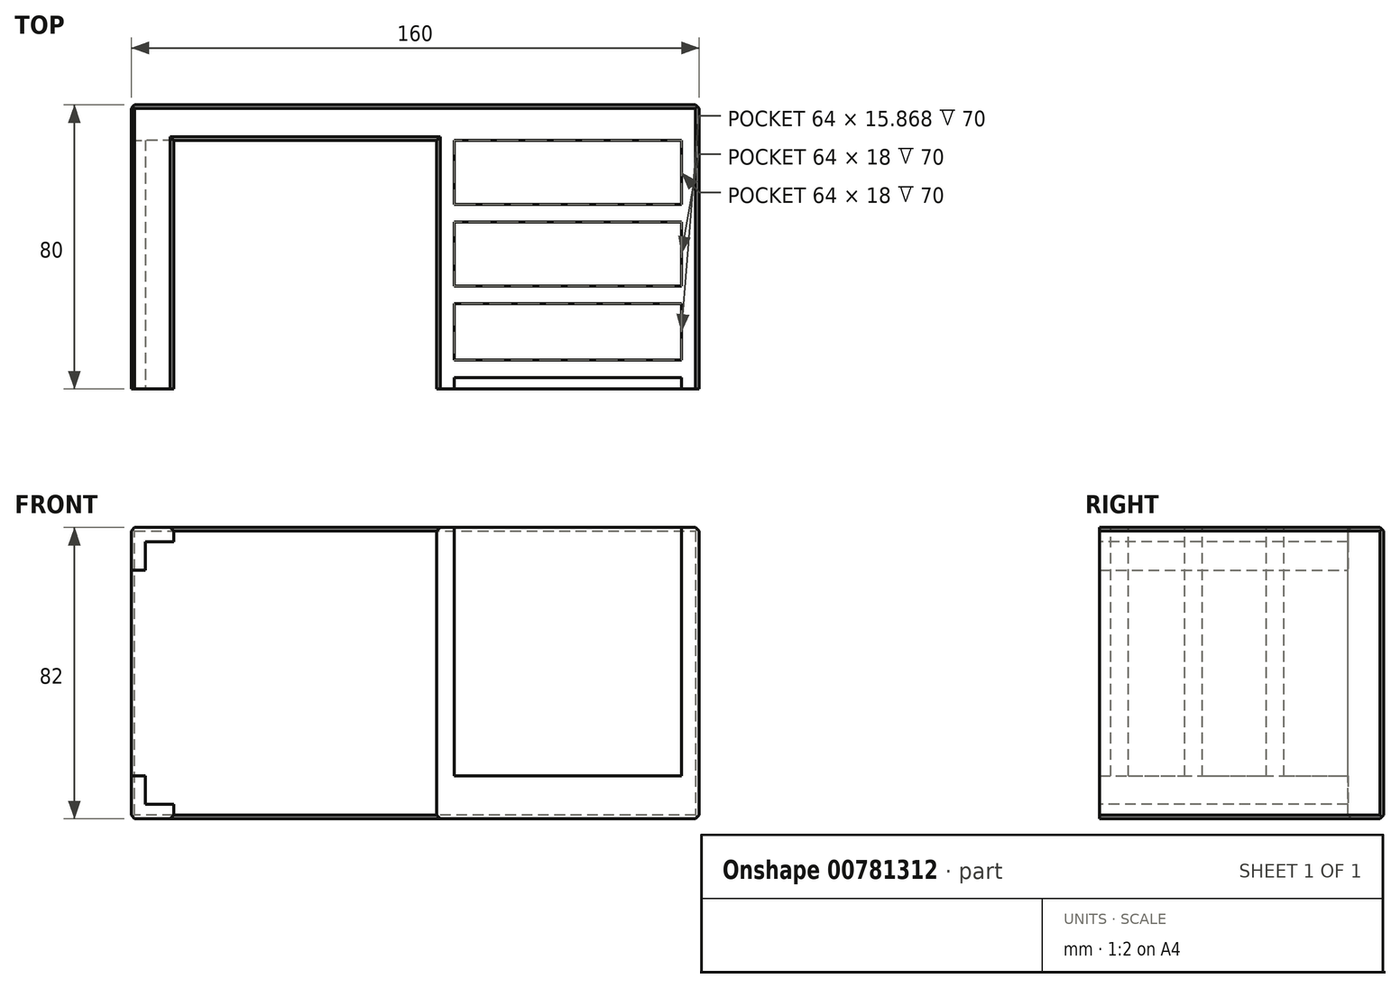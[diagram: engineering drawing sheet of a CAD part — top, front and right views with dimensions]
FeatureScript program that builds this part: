
annotation { "Feature Type Name" : "Feature", "Feature Type Description" : "" }
export const myFeature = defineFeature(function(context is Context, id is Id, definition is map)
    precondition{}
    {
        {
            var Q0;
            Q0=qCreatedBy(makeId("Front.planeOp"),FACE);
            var sketch = newSketch(context, id + "F0", { "sketchPlane" : qUnion([Q0])});
            skLineSegment(sketch, "E0.bottom", {"start": v(80, -41) * mm, "end": v(-80, -41) * mm});
            skLineSegment(sketch, "E0.top", {"start": v(80, 41) * mm, "end": v(-80, 41) * mm});
            skLineSegment(sketch, "E0.left", {"start": v(80, -41) * mm, "end": v(80, 41) * mm});
            skLineSegment(sketch, "E0.right", {"start": v(-80, -41) * mm, "end": v(-80, 41) * mm});
            skPoint(sketch, "E0.middle", {"position": v(0, 0) * mm});
            skSolve(sketch);
        }
        {
            var Q0;
            Q0=makeQuery(id+"F0.imprint","IMPRINT",FACE,{"disambiguationData":[TD([[makeQuery(id+"F0.imprint","IMPRINT",EDGE,{"derivedFrom":sQuery(id+"F0.wireOp",EDGE,"E0.bottom")}),-1.0]])]});
            extrude(context, id + "F1", {"entities" : qUnion([Q0]), "depth" : 10 * mm, "offsetDistance" : 25 * mm});
        }
        {
            var Q0;
            Q0=makeQuery(id+"F1.opExtrude","CAP_FACE",FACE,{"disambiguationData":[OSD([sQuery(id+"F0.wireOp",EDGE,"E0.bottom"),sQuery(id+"F0.wireOp",EDGE,"E0.top"),sQuery(id+"F0.wireOp",EDGE,"E0.left"),sQuery(id+"F0.wireOp",EDGE,"E0.right")])],"isStart":false});
            var sketch = newSketch(context, id + "F2", { "sketchPlane" : qUnion([Q0])});
            skLineSegment(sketch, "E1.bottom", {"start": v(-80, 41) * mm, "end": v(-68, 41) * mm});
            skLineSegment(sketch, "E1.top", {"start": v(-80, 29) * mm, "end": v(-68, 29) * mm});
            skLineSegment(sketch, "E1.left", {"start": v(-80, 41) * mm, "end": v(-80, 29) * mm});
            skLineSegment(sketch, "E1.right", {"start": v(-68, 41) * mm, "end": v(-68, 29) * mm});
            skLineSegment(sketch, "E2.bottom", {"start": v(-80, -41) * mm, "end": v(-68, -41) * mm});
            skLineSegment(sketch, "E2.top", {"start": v(-80, -29) * mm, "end": v(-68, -29) * mm});
            skLineSegment(sketch, "E2.left", {"start": v(-80, -41) * mm, "end": v(-80, -29) * mm});
            skLineSegment(sketch, "E2.right", {"start": v(-68, -41) * mm, "end": v(-68, -29) * mm});
            skSolve(sketch);
        }
        {
            var Q0;
            Q0=makeQuery(id+"F2.imprint","IMPRINT",FACE,{"disambiguationData":[TD([[makeQuery(id+"F2.imprint","IMPRINT",EDGE,{"derivedFrom":sQuery(id+"F2.wireOp",EDGE,"E1.bottom")}),1.0]])]});
            var Q1;
            Q1=makeQuery(id+"F2.imprint","IMPRINT",FACE,{"disambiguationData":[TD([[makeQuery(id+"F2.imprint","IMPRINT",EDGE,{"derivedFrom":sQuery(id+"F2.wireOp",EDGE,"E2.bottom")}),-1.0]])]});
            extrude(context, id + "F3", {"entities" : qUnion([Q0, Q1]), "operationType" : NewBodyOperationType.ADD, "depth" : 70 * mm, "offsetDistance" : 25 * mm});
        }
        {
            var Q0;
            Q0=makeQuery(id+"F1.opExtrude","CAP_FACE",FACE,{"disambiguationData":[OSD([sQuery(id+"F0.wireOp",EDGE,"E0.bottom"),sQuery(id+"F0.wireOp",EDGE,"E0.top"),sQuery(id+"F0.wireOp",EDGE,"E0.left"),sQuery(id+"F0.wireOp",EDGE,"E0.right")])],"isStart":false});
            var sketch = newSketch(context, id + "F4", { "sketchPlane" : qUnion([Q0])});
            skPoint(sketch, "E3.oppositeSnap0", {"position": v(6, -41) * mm});
            skLineSegment(sketch, "E3.bottom", {"start": v(80, -41) * mm, "end": v(6, -41) * mm});
            skLineSegment(sketch, "E3.top", {"start": v(80, -29) * mm, "end": v(6, -29) * mm});
            skLineSegment(sketch, "E3.left", {"start": v(80, -41) * mm, "end": v(80, -29) * mm});
            skLineSegment(sketch, "E3.right", {"start": v(6, -41) * mm, "end": v(6, -29) * mm});
            skSolve(sketch);
        }
        {
            var Q0;
            Q0=makeQuery(id+"F4.imprint","IMPRINT",FACE,{"disambiguationData":[TD([[makeQuery(id+"F4.imprint","IMPRINT",EDGE,{"derivedFrom":sQuery(id+"F4.wireOp",EDGE,"E3.bottom")}),-1.0]])]});
            extrude(context, id + "F5", {"entities" : qUnion([Q0]), "operationType" : NewBodyOperationType.ADD, "depth" : 70 * mm, "offsetDistance" : 25 * mm});
        }
        {
            var Q0;
            Q0=makeQuery(id+"F1.opExtrude","CAP_FACE",FACE,{"disambiguationData":[OSD([sQuery(id+"F0.wireOp",EDGE,"E0.bottom"),sQuery(id+"F0.wireOp",EDGE,"E0.top"),sQuery(id+"F0.wireOp",EDGE,"E0.left"),sQuery(id+"F0.wireOp",EDGE,"E0.right")])],"isStart":false});
            var sketch = newSketch(context, id + "F6", { "sketchPlane" : qUnion([Q0])});
            skLineSegment(sketch, "E4.bottom", {"start": v(6, -29) * mm, "end": v(11, -29) * mm});
            skLineSegment(sketch, "E4.top", {"start": v(6, 41) * mm, "end": v(11, 41) * mm});
            skLineSegment(sketch, "E4.left", {"start": v(6, -29) * mm, "end": v(6, 41) * mm});
            skLineSegment(sketch, "E4.right", {"start": v(11, -29) * mm, "end": v(11, 41) * mm});
            skLineSegment(sketch, "E5.bottom", {"start": v(80, -29) * mm, "end": v(75, -29) * mm});
            skLineSegment(sketch, "E5.top", {"start": v(80, 41) * mm, "end": v(75, 41) * mm});
            skLineSegment(sketch, "E5.left", {"start": v(80, -29) * mm, "end": v(80, 41) * mm});
            skLineSegment(sketch, "E5.right", {"start": v(75, -29) * mm, "end": v(75, 41) * mm});
            skSolve(sketch);
        }
        {
            var Q0;
            Q0=makeQuery(id+"F6.imprint","IMPRINT",FACE,{"disambiguationData":[TD([[makeQuery(id+"F6.imprint","IMPRINT",EDGE,{"derivedFrom":sQuery(id+"F6.wireOp",EDGE,"E4.bottom")}),-1.0]])]});
            var Q1;
            Q1=makeQuery(id+"F6.imprint","IMPRINT",FACE,{"disambiguationData":[TD([[makeQuery(id+"F6.imprint","IMPRINT",EDGE,{"derivedFrom":sQuery(id+"F6.wireOp",EDGE,"E5.bottom")}),-1.0]])]});
            extrude(context, id + "F7", {"entities" : qUnion([Q0, Q1]), "operationType" : NewBodyOperationType.ADD, "depth" : 70 * mm, "offsetDistance" : 25 * mm});
        }
        {
            var Q0;
            Q0=makeQuery(id+"F7.boolean.opBoolean","MERGE",FACE,{"derivedFrom":[makeQuery(id+"F3.boolean.opBoolean","MERGE",FACE,{"derivedFrom":[makeQuery(id+"F1.opExtrude","SWEPT_FACE",FACE,{"disambiguationData":[OSD([sQuery(id+"F0.wireOp",EDGE,"E0.top")])]}),makeQuery(id+"F3.opExtrude","SWEPT_FACE",FACE,{"disambiguationData":[OSD([sQuery(id+"F2.wireOp",EDGE,"E1.bottom")])]})]}),makeQuery(id+"F7.opExtrude","SWEPT_FACE",FACE,{"disambiguationData":[OSD([sQuery(id+"F6.wireOp",EDGE,"E4.top")])]}),makeQuery(id+"F7.opExtrude","SWEPT_FACE",FACE,{"disambiguationData":[OSD([sQuery(id+"F6.wireOp",EDGE,"E5.top")])]})]});
            var sketch = newSketch(context, id + "F8", { "sketchPlane" : qUnion([Q0])});
            skLineSegment(sketch, "E6.bottom", {"start": v(11, -33) * mm, "end": v(75, -33) * mm});
            skLineSegment(sketch, "E6.top", {"start": v(11, -28) * mm, "end": v(75, -28) * mm});
            skLineSegment(sketch, "E6.left", {"start": v(11, -28) * mm, "end": v(11, -33) * mm});
            skLineSegment(sketch, "E6.right", {"start": v(75, -28) * mm, "end": v(75, -33) * mm});
            skLineSegment(sketch, "E7.bottom", {"start": v(11, -56) * mm, "end": v(75, -56) * mm});
            skLineSegment(sketch, "E7.top", {"start": v(11, -51) * mm, "end": v(75, -51) * mm});
            skLineSegment(sketch, "E7.left", {"start": v(11, -51) * mm, "end": v(11, -56) * mm});
            skLineSegment(sketch, "E7.right", {"start": v(75, -51) * mm, "end": v(75, -56) * mm});
            skLineSegment(sketch, "E8.bottom", {"start": v(11, -71.87) * mm, "end": v(75, -71.87) * mm});
            skLineSegment(sketch, "E8.top", {"start": v(11, -76.87) * mm, "end": v(75, -76.87) * mm});
            skLineSegment(sketch, "E8.left", {"start": v(11, -71.87) * mm, "end": v(11, -76.87) * mm});
            skLineSegment(sketch, "E8.right", {"start": v(75, -71.87) * mm, "end": v(75, -76.87) * mm});
            skSolve(sketch);
        }
        {
            var Q0;
            Q0=makeQuery(id+"F8.imprint","IMPRINT",FACE,{"disambiguationData":[TD([[makeQuery(id+"F8.imprint","IMPRINT",EDGE,{"derivedFrom":sQuery(id+"F8.wireOp",EDGE,"E6.bottom")}),1.0]])]});
            var Q1;
            Q1=makeQuery(id+"F8.imprint","IMPRINT",FACE,{"disambiguationData":[TD([[makeQuery(id+"F8.imprint","IMPRINT",EDGE,{"derivedFrom":sQuery(id+"F8.wireOp",EDGE,"E7.bottom")}),1.0]])]});
            var Q2;
            Q2=makeQuery(id+"F8.imprint","IMPRINT",FACE,{"disambiguationData":[TD([[makeQuery(id+"F8.imprint","IMPRINT",EDGE,{"derivedFrom":sQuery(id+"F8.wireOp",EDGE,"E8.bottom")}),-1.0]])]});
            extrude(context, id + "F9", {"entities" : qUnion([Q0, Q1, Q2]), "operationType" : NewBodyOperationType.ADD, "oppositeDirection" : true, "depth" : 80 * mm, "offsetDistance" : 25 * mm});
        }
        {
            var Q0;
            Q0=makeQuery(id+"F3.opExtrude","CAP_FACE",FACE,{"disambiguationData":[OSD([sQuery(id+"F2.wireOp",EDGE,"E1.bottom"),sQuery(id+"F2.wireOp",EDGE,"E1.top"),sQuery(id+"F2.wireOp",EDGE,"E1.left"),sQuery(id+"F2.wireOp",EDGE,"E1.right")])],"isStart":false});
            var sketch = newSketch(context, id + "F10", { "sketchPlane" : qUnion([Q0])});
            skLineSegment(sketch, "E9.bottom", {"start": v(-68, 37) * mm, "end": v(-76, 37) * mm});
            skLineSegment(sketch, "E9.top", {"start": v(-68, 29) * mm, "end": v(-76, 29) * mm});
            skLineSegment(sketch, "E9.left", {"start": v(-68, 37) * mm, "end": v(-68, 29) * mm});
            skLineSegment(sketch, "E9.right", {"start": v(-76, 37) * mm, "end": v(-76, 29) * mm});
            skSolve(sketch);
        }
        {
            var Q0;
            Q0=makeQuery(id+"F10.imprint","IMPRINT",FACE,{"disambiguationData":[TD([[makeQuery(id+"F10.imprint","IMPRINT",EDGE,{"derivedFrom":sQuery(id+"F10.wireOp",EDGE,"E9.bottom")}),1.0]])]});
            extrude(context, id + "F11", {"entities" : qUnion([Q0]), "operationType" : NewBodyOperationType.REMOVE, "oppositeDirection" : true, "depth" : 70 * mm, "offsetDistance" : 25 * mm});
        }
        {
            var Q0;
            Q0=makeQuery(id+"F3.opExtrude","CAP_FACE",FACE,{"disambiguationData":[OSD([sQuery(id+"F2.wireOp",EDGE,"E2.bottom"),sQuery(id+"F2.wireOp",EDGE,"E2.top"),sQuery(id+"F2.wireOp",EDGE,"E2.left"),sQuery(id+"F2.wireOp",EDGE,"E2.right")])],"isStart":false});
            var sketch = newSketch(context, id + "F12", { "sketchPlane" : qUnion([Q0])});
            skLineSegment(sketch, "E10.bottom", {"start": v(-68, -29) * mm, "end": v(-76, -29) * mm});
            skLineSegment(sketch, "E10.top", {"start": v(-68, -37) * mm, "end": v(-76, -37) * mm});
            skLineSegment(sketch, "E10.left", {"start": v(-68, -29) * mm, "end": v(-68, -37) * mm});
            skLineSegment(sketch, "E10.right", {"start": v(-76, -29) * mm, "end": v(-76, -37) * mm});
            skSolve(sketch);
        }
        {
            var Q0;
            Q0=makeQuery(id+"F12.imprint","IMPRINT",FACE,{"disambiguationData":[TD([[makeQuery(id+"F12.imprint","IMPRINT",EDGE,{"derivedFrom":sQuery(id+"F12.wireOp",EDGE,"E10.bottom")}),-1.0]])]});
            extrude(context, id + "F13", {"entities" : qUnion([Q0]), "operationType" : NewBodyOperationType.REMOVE, "oppositeDirection" : true, "depth" : 70 * mm, "offsetDistance" : 25 * mm});
        }
        {
            var Q0;
            Q0=makeQuery(id+"F1.opExtrude","CAP_EDGE",EDGE,{"disambiguationData":[OSD([sQuery(id+"F0.wireOp",EDGE,"E0.right")])],"isStart":true});
            chamfer(context, id + "F14", {"entities" : qUnion([Q0]), "width" : 1 * mm, "tangentPropagation" : true});
        }
        {
            var Q0;
            Q0=makeQuery(id+"F1.opExtrude","CAP_EDGE",EDGE,{"disambiguationData":[OSD([sQuery(id+"F0.wireOp",EDGE,"E0.top")])],"isStart":true});
            chamfer(context, id + "F15", {"entities" : qUnion([Q0]), "width" : 1 * mm, "tangentPropagation" : true});
        }
        {
            var Q0;
            Q0=makeQuery(id+"F1.opExtrude","CAP_EDGE",EDGE,{"disambiguationData":[OSD([sQuery(id+"F0.wireOp",EDGE,"E0.left")])],"isStart":true});
            chamfer(context, id + "F16", {"entities" : qUnion([Q0]), "width" : 1 * mm, "tangentPropagation" : true});
        }
        {
            var Q0;
            Q0=makeQuery(id+"F1.opExtrude","CAP_EDGE",EDGE,{"disambiguationData":[OSD([sQuery(id+"F0.wireOp",EDGE,"E0.bottom")])],"isStart":true});
            chamfer(context, id + "F17", {"entities" : qUnion([Q0]), "width" : 1 * mm, "tangentPropagation" : true});
        }
        {
            var Q0;
            Q0=makeQuery(id+"F3.boolean.opBoolean","MERGE",EDGE,{"derivedFrom":[makeQuery(id+"F1.opExtrude","SWEPT_EDGE",EDGE,{"disambiguationData":[OSD([sQuery(id+"F0.wireOp",EDGE,"E0.top"),sQuery(id+"F0.wireOp",EDGE,"E0.right")])]}),makeQuery(id+"F3.opExtrude","SWEPT_EDGE",EDGE,{"disambiguationData":[OSD([sQuery(id+"F2.wireOp",EDGE,"E1.bottom"),sQuery(id+"F2.wireOp",EDGE,"E1.left")])]})]});
            chamfer(context, id + "F18", {"entities" : qUnion([Q0]), "width" : 1 * mm, "tangentPropagation" : true});
        }
        {
            var Q0;
            Q0=makeQuery(id+"F7.boolean.opBoolean","MERGE",EDGE,{"derivedFrom":[makeQuery(id+"F1.opExtrude","SWEPT_EDGE",EDGE,{"disambiguationData":[OSD([sQuery(id+"F0.wireOp",EDGE,"E0.top"),sQuery(id+"F0.wireOp",EDGE,"E0.left")])]}),makeQuery(id+"F7.opExtrude","SWEPT_EDGE",EDGE,{"disambiguationData":[OSD([sQuery(id+"F6.wireOp",EDGE,"E5.top"),sQuery(id+"F6.wireOp",EDGE,"E5.left")])]})]});
            chamfer(context, id + "F19", {"entities" : qUnion([Q0]), "width" : 1 * mm, "tangentPropagation" : true});
        }
        {
            var Q0;
            Q0=makeQuery(id+"F3.boolean.opBoolean","MERGE",EDGE,{"derivedFrom":[makeQuery(id+"F1.opExtrude","SWEPT_EDGE",EDGE,{"disambiguationData":[OSD([sQuery(id+"F0.wireOp",EDGE,"E0.bottom"),sQuery(id+"F0.wireOp",EDGE,"E0.right")])]}),makeQuery(id+"F3.opExtrude","SWEPT_EDGE",EDGE,{"disambiguationData":[OSD([sQuery(id+"F2.wireOp",EDGE,"E2.bottom"),sQuery(id+"F2.wireOp",EDGE,"E2.left")])]})]});
            chamfer(context, id + "F20", {"entities" : qUnion([Q0]), "width" : 1 * mm, "tangentPropagation" : true});
        }
        {
            var Q0;
            Q0=makeQuery(id+"F5.boolean.opBoolean","MERGE",EDGE,{"derivedFrom":[makeQuery(id+"F1.opExtrude","SWEPT_EDGE",EDGE,{"disambiguationData":[OSD([sQuery(id+"F0.wireOp",EDGE,"E0.bottom"),sQuery(id+"F0.wireOp",EDGE,"E0.left")])]}),makeQuery(id+"F5.opExtrude","SWEPT_EDGE",EDGE,{"disambiguationData":[OSD([sQuery(id+"F4.wireOp",EDGE,"E3.bottom"),sQuery(id+"F4.wireOp",EDGE,"E3.left")])]})]});
            chamfer(context, id + "F21", {"entities" : qUnion([Q0]), "width" : 1 * mm, "tangentPropagation" : true});
        }
        {
            var Q0;
            Q0=makeQuery(id+"F5.opExtrude","SWEPT_EDGE",EDGE,{"disambiguationData":[OSD([sQuery(id+"F0.wireOp",EDGE,"E0.bottom"),sQuery(id+"F4.wireOp",EDGE,"E3.bottom"),sQuery(id+"F4.wireOp",EDGE,"E3.right")])]});
            chamfer(context, id + "F22", {"entities" : qUnion([Q0]), "width" : 1 * mm, "tangentPropagation" : true});
        }
        {
            var Q0;
            Q0=makeQuery(id+"F1.opExtrude","CAP_EDGE",EDGE,{"disambiguationData":[OSD([sQuery(id+"F0.wireOp",EDGE,"E0.bottom")])],"isStart":false});
            chamfer(context, id + "F23", {"entities" : qUnion([Q0]), "width" : 1 * mm, "tangentPropagation" : true});
        }
        {
            var Q0;
            Q0=makeQuery(id+"F3.opExtrude","SWEPT_EDGE",EDGE,{"disambiguationData":[OSD([sQuery(id+"F0.wireOp",EDGE,"E0.bottom"),sQuery(id+"F2.wireOp",EDGE,"E2.bottom"),sQuery(id+"F2.wireOp",EDGE,"E2.right")])]});
            chamfer(context, id + "F24", {"entities" : qUnion([Q0]), "width" : 1 * mm, "tangentPropagation" : true});
        }
        {
            var Q0;
            {var subQ0=sQuery(id+"F0.wireOp",EDGE,"E0.top");Q0=makeQuery(id+"F7.boolean.opBoolean","SPLIT",EDGE,{"disambiguationData":[TD([makeQuery(id+"F3.opExtrude","SWEPT_FACE",FACE,{"disambiguationData":[OSD([sQuery(id+"F2.wireOp",EDGE,"E1.right")])]})])],"derivedFrom":makeQuery(id+"F1.opExtrude","CAP_EDGE",EDGE,{"disambiguationData":[OSD([subQ0])],"isStart":false})});}
            chamfer(context, id + "F25", {"entities" : qUnion([Q0]), "width" : 1 * mm, "tangentPropagation" : true});
        }
        {
            var Q0;
            Q0=makeQuery(id+"F3.opExtrude","SWEPT_EDGE",EDGE,{"disambiguationData":[OSD([sQuery(id+"F0.wireOp",EDGE,"E0.top"),sQuery(id+"F2.wireOp",EDGE,"E1.bottom"),sQuery(id+"F2.wireOp",EDGE,"E1.right")])]});
            chamfer(context, id + "F26", {"entities" : qUnion([Q0]), "width" : 1 * mm, "tangentPropagation" : true});
        }
        {
            var Q0;
            Q0=makeQuery(id+"F7.opExtrude","SWEPT_EDGE",EDGE,{"disambiguationData":[OSD([sQuery(id+"F0.wireOp",EDGE,"E0.top"),sQuery(id+"F6.wireOp",EDGE,"E4.top"),sQuery(id+"F6.wireOp",EDGE,"E4.left")])]});
            chamfer(context, id + "F27", {"entities" : qUnion([Q0]), "width" : 1 * mm, "tangentPropagation" : true});
        }
    });
